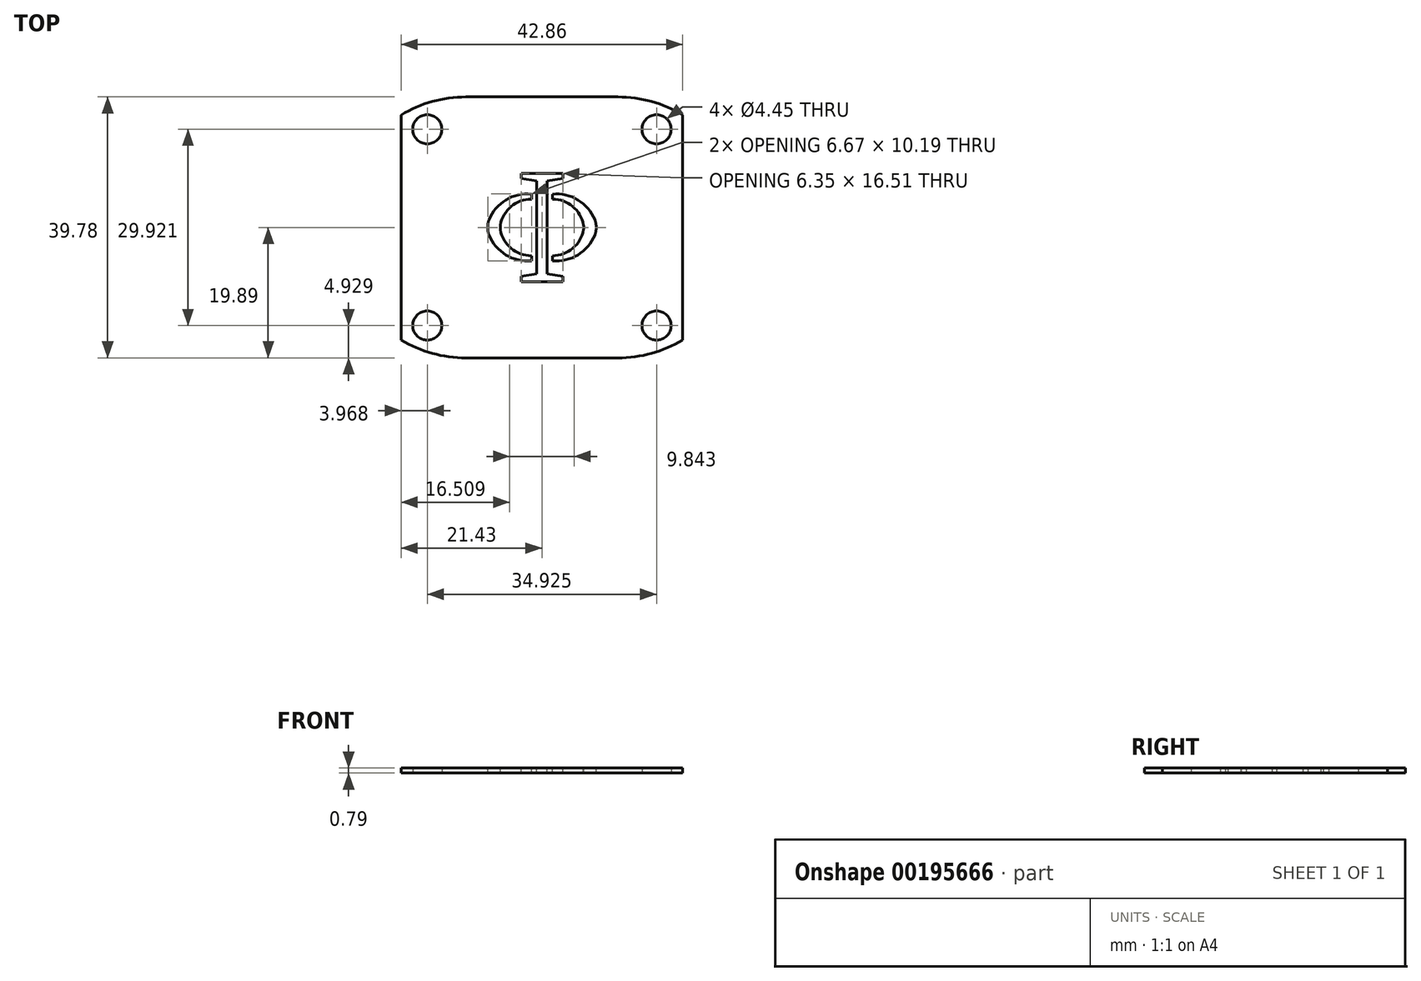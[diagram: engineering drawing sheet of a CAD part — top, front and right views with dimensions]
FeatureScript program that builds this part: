
annotation { "Feature Type Name" : "Feature", "Feature Type Description" : "" }
export const myFeature = defineFeature(function(context is Context, id is Id, definition is map)
    precondition{}
    {
        {
            var Q0;
            Q0=qCreatedBy(makeId("Top.planeOp"),FACE);
            var sketch = newSketch(context, id + "F0", { "sketchPlane" : qUnion([Q0])});
            skLineSegment(sketch, "E0", {"start": v(-21.43, 0) * mm, "end": v(-21.43, 17.14) * mm});
            skLineSegment(sketch, "E1", {"start": v(21.43, 0) * mm, "end": v(21.43, 17.15) * mm});
            skArc(sketch, "E2", {"start": v(-11.58, 19.89) * mm, "mid": v(-16.7, 19.19) * mm, "end": v(-21.43, 17.14) * mm});
            skArc(sketch, "E3", {"start": v(21.43, 17.14) * mm, "mid": v(16.7, 19.19) * mm, "end": v(11.58, 19.89) * mm});
            skLineSegment(sketch, "E4", {"start": v(-11.58, 19.89) * mm, "end": v(0, 19.89) * mm});
            skLineSegment(sketch, "E5", {"start": v(0, 19.89) * mm, "end": v(11.58, 19.89) * mm});
            skLineSegment(sketch, "E6", {"start": v(-39.62, 0) * mm, "end": v(36.58, 0) * mm, "construction": true});
            skLineSegment(sketch, "E7.MirrorCS", {"start": v(-21.43, 0) * mm, "end": v(-21.43, -17.15) * mm});
            skLineSegment(sketch, "E8.MirrorCS", {"start": v(21.43, 0) * mm, "end": v(21.43, -17.15) * mm});
            skLineSegment(sketch, "E9.MirrorCS", {"start": v(-11.58, -19.89) * mm, "end": v(0, -19.89) * mm});
            skLineSegment(sketch, "E10.MirrorCS", {"start": v(0, -19.89) * mm, "end": v(11.58, -19.89) * mm});
            skArc(sketch, "E11.MirrorCS", {"start": v(-11.58, -19.89) * mm, "mid": v(-16.7, -19.19) * mm, "end": v(-21.43, -17.15) * mm});
            skArc(sketch, "E12.MirrorCS", {"start": v(21.43, -17.15) * mm, "mid": v(16.7, -19.19) * mm, "end": v(11.58, -19.89) * mm});
            skCircle(sketch, "E13", {"center": v(-17.46, 14.96) * mm, "radius": 2.22 * mm});
            skCircle(sketch, "E14.1.0.0", {"center": v(17.46, 14.96) * mm, "radius": 2.22 * mm});
            skLineSegment(sketch, "E14.direction1", {"start": v(-17.46, 14.96) * mm, "end": v(17.46, 14.96) * mm, "construction": true});
            skCircle(sketch, "E15.MirrorC", {"center": v(-17.46, -14.96) * mm, "radius": 2.22 * mm});
            skCircle(sketch, "E16.MirrorC", {"center": v(17.46, -14.96) * mm, "radius": 2.22 * mm});
            skSolve(sketch);
        }
        {
            var Q0;
            Q0 = qSketchRegion(id + "F0", true);
            extrude(context, id + "F1", {"entities" : qUnion([Q0]), "depth" : 0.8 * mm});
        }
        {
            var Q0;
            Q0=makeQuery(id+"F1.opExtrude","CAP_FACE",FACE,{"disambiguationData":[OSD([sQuery(id+"F0.wireOp",EDGE,"E0"),sQuery(id+"F0.wireOp",EDGE,"E1"),sQuery(id+"F0.wireOp",EDGE,"E2"),sQuery(id+"F0.wireOp",EDGE,"E3"),sQuery(id+"F0.wireOp",EDGE,"E4"),sQuery(id+"F0.wireOp",EDGE,"E5"),sQuery(id+"F0.wireOp",EDGE,"E7.MirrorCS"),sQuery(id+"F0.wireOp",EDGE,"E8.MirrorCS"),sQuery(id+"F0.wireOp",EDGE,"E9.MirrorCS"),sQuery(id+"F0.wireOp",EDGE,"E10.MirrorCS"),sQuery(id+"F0.wireOp",EDGE,"E11.MirrorCS"),sQuery(id+"F0.wireOp",EDGE,"E12.MirrorCS"),sQuery(id+"F0.wireOp",EDGE,"E14.1.0.0"),sQuery(id+"F0.wireOp",EDGE,"E15.MirrorC"),sQuery(id+"F0.wireOp",EDGE,"E16.MirrorC"),sQuery(id+"F0.wireOp",EDGE,"E13")])],"isStart":false});
            var sketch = newSketch(context, id + "F2", { "sketchPlane" : qUnion([Q0])});
            skLineSegment(sketch, "E17", {"start": v(0, 8.26) * mm, "end": v(3.18, 8.26) * mm});
            skLineSegment(sketch, "E18", {"start": v(3.18, 8.26) * mm, "end": v(3.18, 7.46) * mm});
            skLineSegment(sketch, "E19", {"start": v(3.18, 7.46) * mm, "end": v(0.8, 7.08) * mm});
            skLineSegment(sketch, "E20", {"start": v(0.8, 7.08) * mm, "end": v(0.8, 0) * mm});
            skLineSegment(sketch, "E21", {"start": v(-6.42, 0) * mm, "end": v(5.6, 0) * mm, "construction": true});
            skLineSegment(sketch, "E22", {"start": v(0, 10.23) * mm, "end": v(0, -10.08) * mm, "construction": true});
            skLineSegment(sketch, "E23", {"start": v(6.35, 0) * mm, "end": v(6.35, 0.18) * mm});
            skLineSegment(sketch, "E24", {"start": v(8.26, 0) * mm, "end": v(8.26, 0.2) * mm});
            skArc(sketch, "E25", {"start": v(8.07, 1.16) * mm, "mid": v(5.47, 4.2) * mm, "end": v(1.59, 5.08) * mm});
            skPoint(sketch, "E26.visualSharp", {"position": v(6.35, 0.25) * mm});
            skArc(sketch, "E26.filletArc", {"start": v(6.35, 0.18) * mm, "mid": v(6.35, 0.26) * mm, "end": v(6.34, 0.34) * mm});
            skPoint(sketch, "E27.visualSharp", {"position": v(8.26, 0.64) * mm});
            skArc(sketch, "E27.filletArc", {"start": v(8.26, 0.2) * mm, "mid": v(8.2, 0.7) * mm, "end": v(8.07, 1.16) * mm});
            skLineSegment(sketch, "E28", {"start": v(1.59, 5.08) * mm, "end": v(1.59, 4.32) * mm});
            skArc(sketch, "E29", {"start": v(6.34, 0.34) * mm, "mid": v(4.69, 3.2) * mm, "end": v(1.59, 4.32) * mm});
            skLineSegment(sketch, "E30.MirrorCS", {"start": v(6.35, 0) * mm, "end": v(6.35, -0.18) * mm});
            skArc(sketch, "E31.MirrorCS", {"start": v(6.35, -0.18) * mm, "mid": v(6.35, -0.26) * mm, "end": v(6.34, -0.34) * mm});
            skLineSegment(sketch, "E32.MirrorCS", {"start": v(8.26, 0) * mm, "end": v(8.26, -0.2) * mm});
            skArc(sketch, "E33.MirrorCS", {"start": v(8.07, -1.16) * mm, "mid": v(5.47, -4.2) * mm, "end": v(1.59, -5.08) * mm});
            skArc(sketch, "E34.MirrorCS", {"start": v(8.26, -0.2) * mm, "mid": v(8.2, -0.7) * mm, "end": v(8.07, -1.16) * mm});
            skArc(sketch, "E35.MirrorCS", {"start": v(6.34, -0.34) * mm, "mid": v(4.69, -3.2) * mm, "end": v(1.59, -4.32) * mm});
            skPoint(sketch, "E36.MirrorP", {"position": v(8.26, -0.64) * mm});
            skPoint(sketch, "E37.MirrorP", {"position": v(6.35, -0.25) * mm});
            skLineSegment(sketch, "E38.MirrorCS", {"start": v(0.8, -7.08) * mm, "end": v(0.8, 0) * mm});
            skLineSegment(sketch, "E39.MirrorCS", {"start": v(0, -8.26) * mm, "end": v(3.18, -8.26) * mm});
            skLineSegment(sketch, "E40.MirrorCS", {"start": v(1.59, -5.08) * mm, "end": v(1.59, -4.32) * mm});
            skLineSegment(sketch, "E41.MirrorCS", {"start": v(3.18, -8.26) * mm, "end": v(3.18, -7.46) * mm});
            skLineSegment(sketch, "E42.MirrorCS", {"start": v(3.18, -7.46) * mm, "end": v(0.8, -7.08) * mm});
            skArc(sketch, "E43.MirrorCS", {"start": v(-6.35, -0.18) * mm, "mid": v(-6.35, -0.26) * mm, "end": v(-6.34, -0.34) * mm});
            skLineSegment(sketch, "E44.MirrorCS", {"start": v(-6.35, 0) * mm, "end": v(-6.35, -0.18) * mm});
            skLineSegment(sketch, "E45.MirrorCS", {"start": v(-6.35, 0) * mm, "end": v(-6.35, 0.18) * mm});
            skArc(sketch, "E46.MirrorCS", {"start": v(-6.35, 0.18) * mm, "mid": v(-6.35, 0.26) * mm, "end": v(-6.34, 0.34) * mm});
            skLineSegment(sketch, "E47.MirrorCS", {"start": v(-8.26, 0) * mm, "end": v(-8.26, -0.2) * mm});
            skLineSegment(sketch, "E48.MirrorCS", {"start": v(-8.26, 0) * mm, "end": v(-8.26, 0.2) * mm});
            skLineSegment(sketch, "E49.MirrorCS", {"start": v(-1.59, -5.08) * mm, "end": v(-1.59, -4.32) * mm});
            skLineSegment(sketch, "E50.MirrorCS", {"start": v(-1.59, 5.08) * mm, "end": v(-1.59, 4.32) * mm});
            skArc(sketch, "E51.MirrorCS", {"start": v(-8.26, -0.2) * mm, "mid": v(-8.2, -0.7) * mm, "end": v(-8.07, -1.16) * mm});
            skArc(sketch, "E52.MirrorCS", {"start": v(-8.26, 0.2) * mm, "mid": v(-8.2, 0.7) * mm, "end": v(-8.07, 1.16) * mm});
            skArc(sketch, "E53.MirrorCS", {"start": v(-8.07, -1.16) * mm, "mid": v(-5.47, -4.2) * mm, "end": v(-1.59, -5.08) * mm});
            skArc(sketch, "E54.MirrorCS", {"start": v(-6.34, -0.34) * mm, "mid": v(-4.69, -3.2) * mm, "end": v(-1.59, -4.32) * mm});
            skLineSegment(sketch, "E55.MirrorCS", {"start": v(-0.8, -7.08) * mm, "end": v(-0.8, 0) * mm});
            skLineSegment(sketch, "E56.MirrorCS", {"start": v(-3.18, 8.26) * mm, "end": v(-3.18, 7.46) * mm});
            skPoint(sketch, "E57.MirrorP", {"position": v(-8.25, 0.64) * mm});
            skLineSegment(sketch, "E58.MirrorCS", {"start": v(-0.8, 7.08) * mm, "end": v(-0.8, 0) * mm});
            skLineSegment(sketch, "E59.MirrorCS", {"start": v(0, -8.26) * mm, "end": v(-3.18, -8.26) * mm});
            skLineSegment(sketch, "E60.MirrorCS", {"start": v(-3.18, -8.26) * mm, "end": v(-3.18, -7.46) * mm});
            skLineSegment(sketch, "E61.MirrorCS", {"start": v(0, 8.26) * mm, "end": v(-3.18, 8.26) * mm});
            skPoint(sketch, "E62.MirrorP", {"position": v(-6.35, 0.25) * mm});
            skArc(sketch, "E63.MirrorCS", {"start": v(-6.34, 0.34) * mm, "mid": v(-4.69, 3.2) * mm, "end": v(-1.59, 4.32) * mm});
            skLineSegment(sketch, "E64.MirrorCS", {"start": v(-3.18, -7.46) * mm, "end": v(-0.8, -7.08) * mm});
            skPoint(sketch, "E65.MirrorP", {"position": v(-6.35, -0.25) * mm});
            skLineSegment(sketch, "E66.MirrorCS", {"start": v(-3.18, 7.46) * mm, "end": v(-0.8, 7.08) * mm});
            skLineSegment(sketch, "E67.MirrorCS", {"start": v(6.42, 0) * mm, "end": v(-5.6, 0) * mm, "construction": true});
            skPoint(sketch, "E68.MirrorP", {"position": v(-8.25, -0.64) * mm});
            skArc(sketch, "E69.MirrorCS", {"start": v(-8.07, 1.16) * mm, "mid": v(-5.47, 4.2) * mm, "end": v(-1.59, 5.08) * mm});
            skSolve(sketch);
        }
        {
            var Q0;
            Q0=makeQuery(id+"F2.imprint","IMPRINT",FACE,{"disambiguationData":[TD([[makeQuery(id+"F2.imprint","IMPRINT",EDGE,{"derivedFrom":sQuery(id+"F2.wireOp",EDGE,"E43.MirrorCS")}),-1.0]])]});
            var Q1;
            Q1=makeQuery(id+"F2.imprint","IMPRINT",FACE,{"disambiguationData":[TD([[makeQuery(id+"F2.imprint","IMPRINT",EDGE,{"derivedFrom":sQuery(id+"F2.wireOp",EDGE,"E17")}),-1.0]])]});
            var Q2;
            Q2=makeQuery(id+"F2.imprint","IMPRINT",FACE,{"disambiguationData":[TD([[makeQuery(id+"F2.imprint","IMPRINT",EDGE,{"derivedFrom":sQuery(id+"F2.wireOp",EDGE,"E23")}),-1.0]])]});
            extrude(context, id + "F3", {"entities" : qUnion([Q0, Q1, Q2]), "operationType" : NewBodyOperationType.REMOVE, "oppositeDirection" : true, "depth" : 25.4 * mm});
        }
    });
